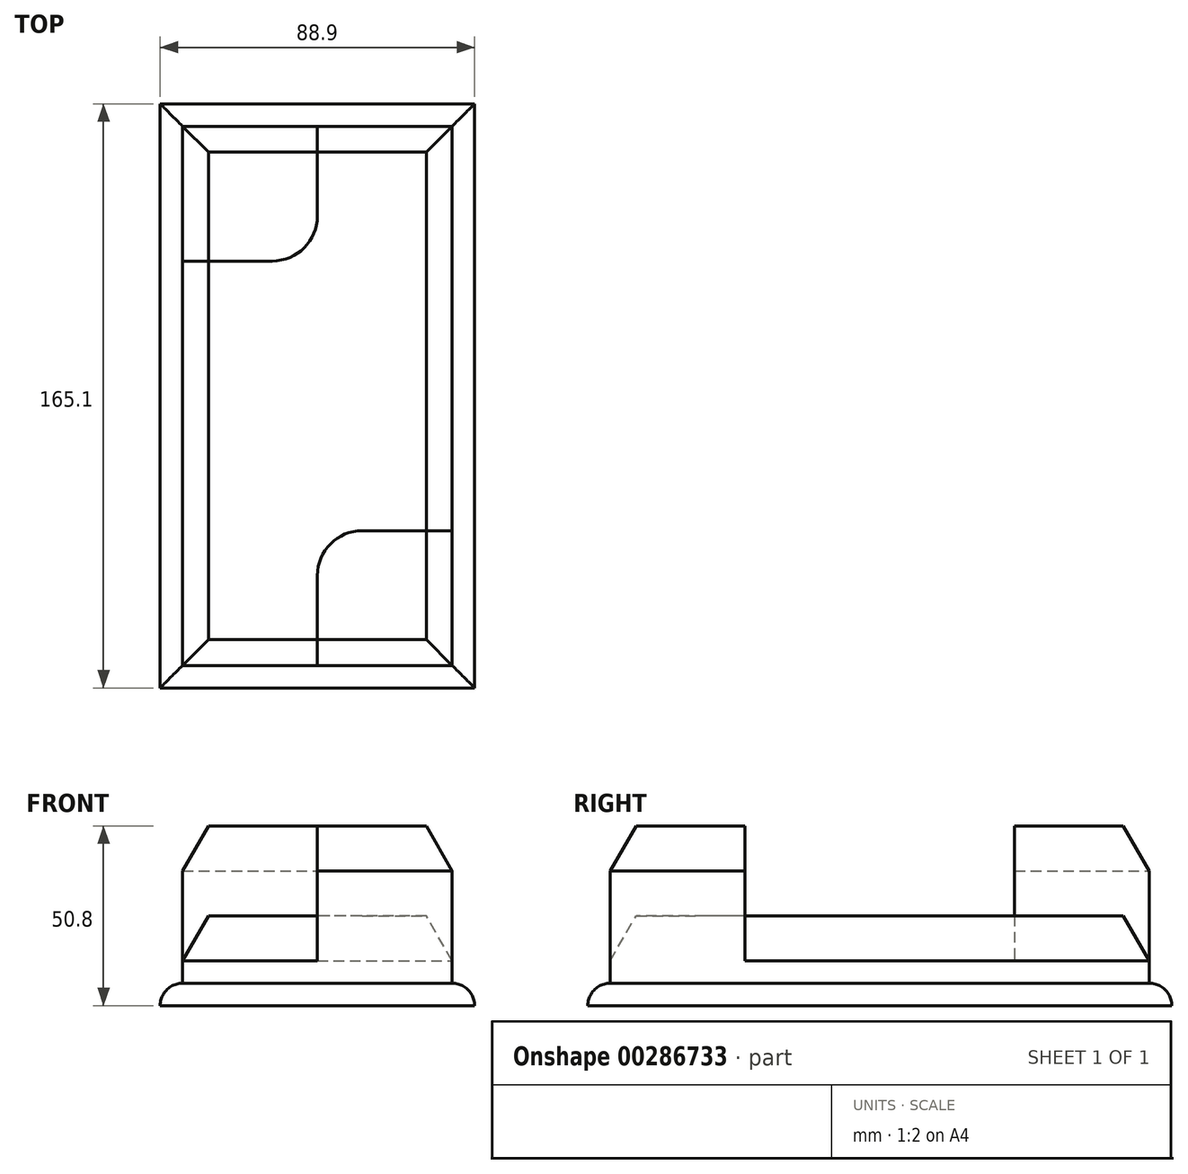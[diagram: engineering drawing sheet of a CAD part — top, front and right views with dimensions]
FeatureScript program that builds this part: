
annotation { "Feature Type Name" : "Feature", "Feature Type Description" : "" }
export const myFeature = defineFeature(function(context is Context, id is Id, definition is map)
    precondition{}
    {
        {
            var Q0;
            Q0=qCreatedBy(makeId("Top.planeOp"),FACE);
            var sketch = newSketch(context, id + "F0", { "sketchPlane" : qUnion([Q0])});
            skLineSegment(sketch, "E0.bottom", {"start": v(38.1, -76.2) * mm, "end": v(-38.1, -76.2) * mm});
            skLineSegment(sketch, "E0.top", {"start": v(38.1, 76.2) * mm, "end": v(-38.1, 76.2) * mm});
            skLineSegment(sketch, "E0.left", {"start": v(38.1, -76.2) * mm, "end": v(38.1, 76.2) * mm});
            skLineSegment(sketch, "E0.right", {"start": v(-38.1, -76.2) * mm, "end": v(-38.1, 76.2) * mm});
            skPoint(sketch, "E0.middle", {"position": v(0, 0) * mm});
            skLineSegment(sketch, "E1.0", {"start": v(44.45, 82.55) * mm, "end": v(-44.45, 82.55) * mm});
            skLineSegment(sketch, "E1.1", {"start": v(44.45, -82.55) * mm, "end": v(44.45, 82.55) * mm});
            skLineSegment(sketch, "E1.2", {"start": v(44.45, -82.55) * mm, "end": v(-44.45, -82.55) * mm});
            skLineSegment(sketch, "E1.3", {"start": v(-44.45, -82.55) * mm, "end": v(-44.45, 82.55) * mm});
            skLineSegment(sketch, "E2", {"start": v(0, 76.2) * mm, "end": v(0, 50.8) * mm});
            skLineSegment(sketch, "E3", {"start": v(-12.7, 38.1) * mm, "end": v(-38.1, 38.1) * mm});
            skLineSegment(sketch, "E4", {"start": v(0, -76.2) * mm, "end": v(0, -50.8) * mm});
            skLineSegment(sketch, "E5", {"start": v(12.7, -38.1) * mm, "end": v(38.1, -38.1) * mm});
            skPoint(sketch, "E6.visualSharp", {"position": v(0, -38.1) * mm});
            skArc(sketch, "E6.filletArc", {"start": v(12.7, -38.1) * mm, "mid": v(3.72, -41.82) * mm, "end": v(0, -50.8) * mm});
            skPoint(sketch, "E7.visualSharp", {"position": v(0, 38.1) * mm});
            skArc(sketch, "E7.filletArc", {"start": v(-12.7, 38.1) * mm, "mid": v(-3.72, 41.82) * mm, "end": v(0, 50.8) * mm});
            skSolve(sketch);
        }
        {
            var Q0;
            Q0=makeQuery(id+"F0.imprint","IMPRINT",FACE,{"disambiguationData":[TD([[makeQuery(id+"F0.imprint","IMPRINT",EDGE,{"derivedFrom":sQuery(id+"F0.wireOp",EDGE,"E1.0")}),1.0]])]});
            extrude(context, id + "F1", {"entities" : qUnion([Q0]), "depth" : 6.35 * mm});
        }
        {
            var Q0;
            {var subQ4=sQuery(id+"F0.wireOp",EDGE,"E2");Q0=makeQuery(id+"F0.imprint","IMPRINT",FACE,{"disambiguationData":[TD([[makeQuery(id+"F0.imprint","IMPRINT",EDGE,{"derivedFrom":subQ4}),1.0]])]});}
            extrude(context, id + "F2", {"entities" : qUnion([Q0]), "operationType" : NewBodyOperationType.ADD, "depth" : 25.4 * mm});
        }
        {
            var Q0;
            {var subQ0=sQuery(id+"F0.wireOp",EDGE,"E2");Q0=makeQuery(id+"F0.imprint","IMPRINT",FACE,{"disambiguationData":[TD([[makeQuery(id+"F0.imprint","IMPRINT",EDGE,{"derivedFrom":subQ0}),-1.0]])]});}
            var Q1;
            {var subQ0=sQuery(id+"F0.wireOp",EDGE,"E4");Q1=makeQuery(id+"F0.imprint","IMPRINT",FACE,{"disambiguationData":[TD([[makeQuery(id+"F0.imprint","IMPRINT",EDGE,{"derivedFrom":subQ0}),-1.0]])]});}
            extrude(context, id + "F3", {"entities" : qUnion([Q0, Q1]), "operationType" : NewBodyOperationType.ADD, "depth" : 50.8 * mm});
        }
        {
            var Q0;
            Q0=makeQuery(id+"F3.opExtrude","CAP_EDGE",EDGE,{"disambiguationData":[OSD([sQuery(id+"F0.wireOp",EDGE,"E0.bottom")])],"isStart":false});
            var Q1;
            Q1=makeQuery(id+"F3.opExtrude","CAP_EDGE",EDGE,{"disambiguationData":[OSD([sQuery(id+"F0.wireOp",EDGE,"E0.left")])],"isStart":false});
            var Q2;
            Q2=makeQuery(id+"F2.opExtrude","CAP_EDGE",EDGE,{"disambiguationData":[OSD([sQuery(id+"F0.wireOp",EDGE,"E0.bottom")])],"isStart":false});
            var Q3;
            Q3=makeQuery(id+"F2.opExtrude","CAP_EDGE",EDGE,{"disambiguationData":[OSD([sQuery(id+"F0.wireOp",EDGE,"E0.right")])],"isStart":false});
            var Q4;
            Q4=makeQuery(id+"F3.opExtrude","CAP_EDGE",EDGE,{"disambiguationData":[OSD([sQuery(id+"F0.wireOp",EDGE,"E0.right")])],"isStart":false});
            chamfer(context, id + "F4", {"entities" : qUnion([Q0, Q1, Q2, Q3, Q4]), "chamferType" : ChamferType.OFFSET_ANGLE, "width" : 12.7 * mm, "oppositeDirection" : false, "angle" : PI / 6 * radian});
        }
        {
            var Q0;
            Q0=makeQuery(id+"F1.opExtrude","CAP_EDGE",EDGE,{"disambiguationData":[OSD([sQuery(id+"F0.wireOp",EDGE,"E1.0")])],"isStart":false});
            var Q1;
            Q1=makeQuery(id+"F1.opExtrude","CAP_EDGE",EDGE,{"disambiguationData":[OSD([sQuery(id+"F0.wireOp",EDGE,"E1.1")])],"isStart":false});
            var Q2;
            Q2=makeQuery(id+"F1.opExtrude","CAP_EDGE",EDGE,{"disambiguationData":[OSD([sQuery(id+"F0.wireOp",EDGE,"E1.3")])],"isStart":false});
            var Q3;
            Q3=makeQuery(id+"F1.opExtrude","CAP_EDGE",EDGE,{"disambiguationData":[OSD([sQuery(id+"F0.wireOp",EDGE,"E1.2")])],"isStart":false});
            fillet(context, id + "F5", {"entities" : qUnion([Q0, Q1, Q2, Q3]), "radius" : 6.35 * mm, "tangentPropagation" : true, "allowEdgeOverflow" : false});
        }
        {
            var Q0;
            Q0=makeQuery(id+"F3.opExtrude","CAP_EDGE",EDGE,{"disambiguationData":[OSD([sQuery(id+"F0.wireOp",EDGE,"E0.top")])],"isStart":false});
            var Q1;
            Q1=makeQuery(id+"F2.opExtrude","CAP_EDGE",EDGE,{"disambiguationData":[OSD([sQuery(id+"F0.wireOp",EDGE,"E0.top")])],"isStart":false});
            var Q2;
            Q2=makeQuery(id+"F2.opExtrude","CAP_EDGE",EDGE,{"disambiguationData":[OSD([sQuery(id+"F0.wireOp",EDGE,"E0.left")])],"isStart":false});
            chamfer(context, id + "F6", {"entities" : qUnion([Q0, Q1, Q2]), "chamferType" : ChamferType.OFFSET_ANGLE, "width" : 12.7 * mm, "oppositeDirection" : true, "angle" : PI / 6 * radian, "tangentPropagation" : true});
        }
    });
